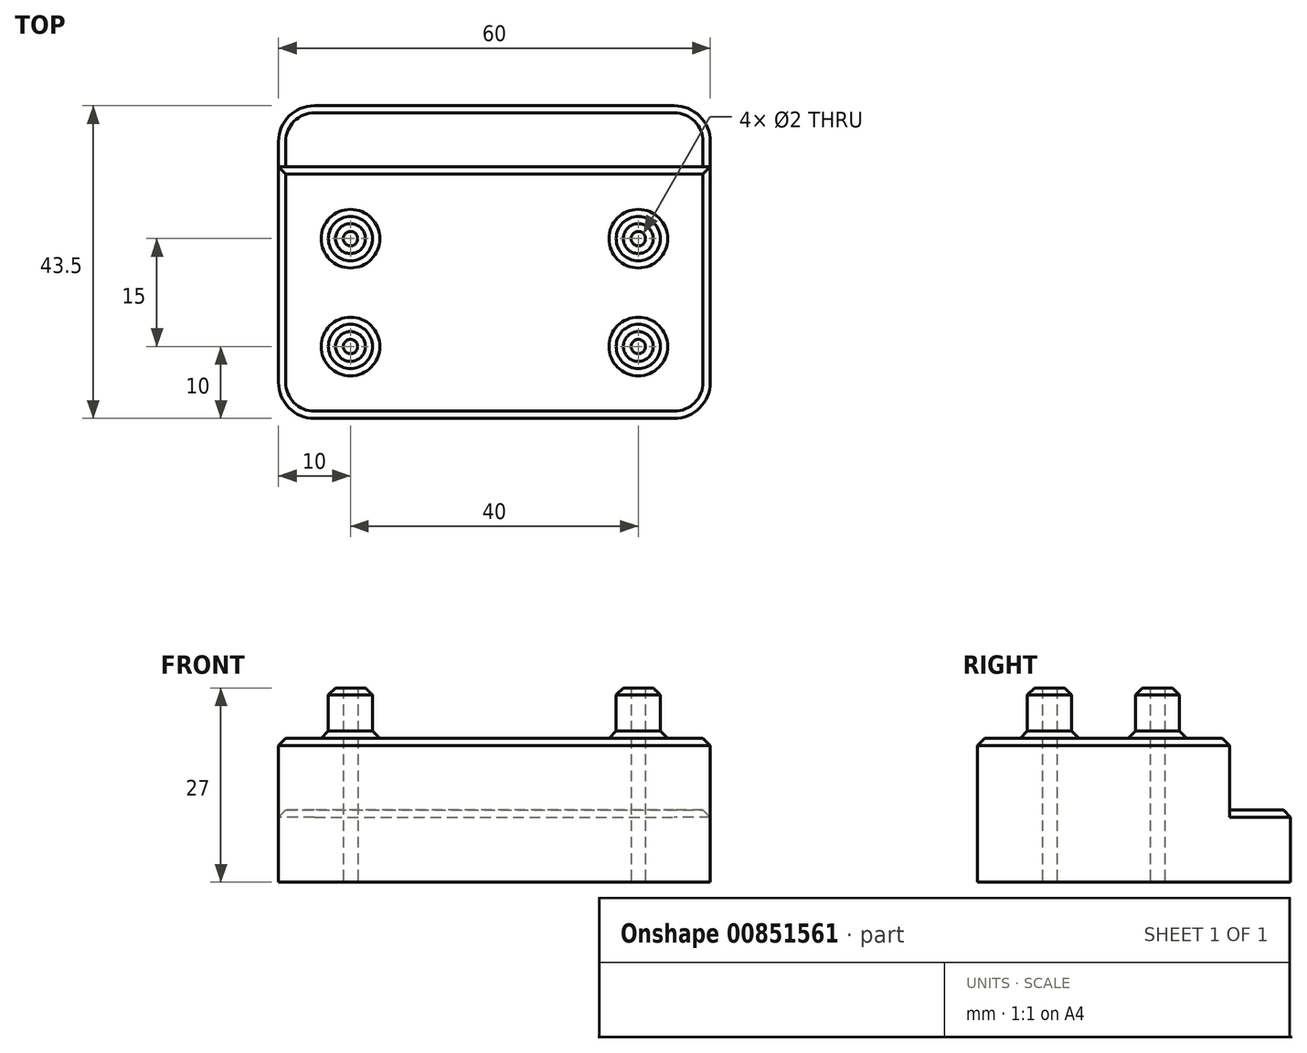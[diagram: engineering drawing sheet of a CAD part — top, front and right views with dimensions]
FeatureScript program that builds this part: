
annotation { "Feature Type Name" : "Feature", "Feature Type Description" : "" }
export const myFeature = defineFeature(function(context is Context, id is Id, definition is map)
    precondition{}
    {
        {
            var Q0;
            Q0=qCreatedBy(makeId("Top.planeOp"),FACE);
            var sketch = newSketch(context, id + "F0", { "sketchPlane" : qUnion([Q0])});
            skLineSegment(sketch, "E0.bottom", {"start": v(0, 0) * mm, "end": v(60, 0) * mm});
            skLineSegment(sketch, "E0.top", {"start": v(0, 43.5) * mm, "end": v(60, 43.5) * mm});
            skLineSegment(sketch, "E0.left", {"start": v(0, 0) * mm, "end": v(0, 43.5) * mm});
            skLineSegment(sketch, "E0.right", {"start": v(60, 0) * mm, "end": v(60, 43.5) * mm});
            skCircle(sketch, "E1", {"center": v(10, 10) * mm, "radius": 3.08 * mm});
            skCircle(sketch, "E2", {"center": v(10, 10) * mm, "radius": 1 * mm});
            skCircle(sketch, "E3.0.1.0", {"center": v(10, 25) * mm, "radius": 1 * mm});
            skCircle(sketch, "E3.0.1.1", {"center": v(10, 25) * mm, "radius": 3.08 * mm});
            skCircle(sketch, "E3.1.0.0", {"center": v(50, 10) * mm, "radius": 1 * mm});
            skCircle(sketch, "E3.1.0.1", {"center": v(50, 10) * mm, "radius": 3.08 * mm});
            skCircle(sketch, "E3.1.1.0", {"center": v(50, 25) * mm, "radius": 1 * mm});
            skCircle(sketch, "E3.1.1.1", {"center": v(50, 25) * mm, "radius": 3.08 * mm});
            skCircle(sketch, "E3.2.0.0", {"center": v(90, 10) * mm, "radius": 1 * mm});
            skCircle(sketch, "E3.2.0.1", {"center": v(90, 10) * mm, "radius": 3.08 * mm});
            skCircle(sketch, "E3.2.1.0", {"center": v(90, 25) * mm, "radius": 1 * mm});
            skCircle(sketch, "E3.2.1.1", {"center": v(90, 25) * mm, "radius": 3.08 * mm});
            skLineSegment(sketch, "E3.direction1", {"start": v(10, 10) * mm, "end": v(50, 10) * mm, "construction": true});
            skLineSegment(sketch, "E3.direction2", {"start": v(10, 10) * mm, "end": v(10, 25) * mm, "construction": true});
            skSolve(sketch);
        }
        {
            var Q0;
            Q0=makeQuery(id+"F0.imprint","IMPRINT",FACE,{"disambiguationData":[TD([[makeQuery(id+"F0.imprint","IMPRINT",EDGE,{"derivedFrom":sQuery(id+"F0.wireOp",EDGE,"E0.bottom")}),1.0]])]});
            extrude(context, id + "F1", {"entities" : qUnion([Q0]), "depth" : 20 * mm, "offsetDistance" : 25 * mm});
        }
        {
            var Q0;
            Q0=makeQuery(id+"F0.imprint","IMPRINT",FACE,{"disambiguationData":[TD([[makeQuery(id+"F0.imprint","IMPRINT",EDGE,{"derivedFrom":sQuery(id+"F0.wireOp",EDGE,"E3.0.1.0")}),-1.0]])]});
            var Q1;
            Q1=makeQuery(id+"F0.imprint","IMPRINT",FACE,{"disambiguationData":[TD([[makeQuery(id+"F0.imprint","IMPRINT",EDGE,{"derivedFrom":sQuery(id+"F0.wireOp",EDGE,"E1")}),1.0]])]});
            var Q2;
            Q2=makeQuery(id+"F0.imprint","IMPRINT",FACE,{"disambiguationData":[TD([[makeQuery(id+"F0.imprint","IMPRINT",EDGE,{"derivedFrom":sQuery(id+"F0.wireOp",EDGE,"E3.1.0.0")}),-1.0]])]});
            var Q3;
            Q3=makeQuery(id+"F0.imprint","IMPRINT",FACE,{"disambiguationData":[TD([[makeQuery(id+"F0.imprint","IMPRINT",EDGE,{"derivedFrom":sQuery(id+"F0.wireOp",EDGE,"E3.1.1.0")}),-1.0]])]});
            var Q4;
            Q4=sQuery(id+"F0.wireOp",EDGE,"E3.0.1.1");
            var Q5;
            Q5=sQuery(id+"F0.wireOp",EDGE,"E1");
            var Q6;
            Q6=sQuery(id+"F0.wireOp",EDGE,"E3.1.0.1");
            var Q7;
            Q7=sQuery(id+"F0.wireOp",EDGE,"E3.1.1.1");
            extrude(context, id + "F2", {"entities" : qUnion([Q0, Q1, Q2, Q3]), "operationType" : NewBodyOperationType.ADD, "surfaceOperationType" : NewSurfaceOperationType.ADD, "surfaceEntities" : qUnion([Q4, Q5, Q6, Q7]), "depth" : 27 * mm, "offsetDistance" : 25 * mm});
        }
        {
            var Q0;
            Q0=makeQuery(id+"F1.opExtrude","CAP_FACE",FACE,{"disambiguationData":[OSD([sQuery(id+"F0.wireOp",EDGE,"E0.bottom"),sQuery(id+"F0.wireOp",EDGE,"E0.top"),sQuery(id+"F0.wireOp",EDGE,"E0.left"),sQuery(id+"F0.wireOp",EDGE,"E0.right"),sQuery(id+"F0.wireOp",EDGE,"E1"),sQuery(id+"F0.wireOp",EDGE,"E3.0.1.1"),sQuery(id+"F0.wireOp",EDGE,"E3.1.0.1"),sQuery(id+"F0.wireOp",EDGE,"E3.1.1.1")])],"isStart":false});
            var sketch = newSketch(context, id + "F3", { "sketchPlane" : qUnion([Q0])});
            skLineSegment(sketch, "E4.bottom", {"start": v(0, 43.5) * mm, "end": v(60, 43.5) * mm});
            skLineSegment(sketch, "E4.top", {"start": v(0, 35) * mm, "end": v(60, 35) * mm});
            skLineSegment(sketch, "E4.left", {"start": v(0, 43.5) * mm, "end": v(0, 35) * mm});
            skLineSegment(sketch, "E4.right", {"start": v(60, 43.5) * mm, "end": v(60, 35) * mm});
            skSolve(sketch);
        }
        {
            var Q0;
            Q0=makeQuery(id+"F3.imprint","IMPRINT",FACE,{"disambiguationData":[TD([[makeQuery(id+"F3.imprint","IMPRINT",EDGE,{"derivedFrom":sQuery(id+"F3.wireOp",EDGE,"E4.bottom")}),-1.0]])]});
            extrude(context, id + "F4", {"entities" : qUnion([Q0]), "operationType" : NewBodyOperationType.REMOVE, "oppositeDirection" : true, "depth" : 10 * mm, "offsetDistance" : 25 * mm});
        }
        {
            var Q0;
            Q0=makeQuery(id+"F1.opExtrude","SWEPT_EDGE",EDGE,{"disambiguationData":[OSD([sQuery(id+"F0.wireOp",EDGE,"E0.bottom"),sQuery(id+"F0.wireOp",EDGE,"E0.right")])]});
            var Q1;
            Q1=makeQuery(id+"F1.opExtrude","SWEPT_EDGE",EDGE,{"disambiguationData":[OSD([sQuery(id+"F0.wireOp",EDGE,"E0.bottom"),sQuery(id+"F0.wireOp",EDGE,"E0.left")])]});
            var Q2;
            Q2=makeQuery(id+"F1.opExtrude","SWEPT_EDGE",EDGE,{"disambiguationData":[OSD([sQuery(id+"F0.wireOp",EDGE,"E0.top"),sQuery(id+"F0.wireOp",EDGE,"E0.right")])]});
            var Q3;
            Q3=makeQuery(id+"F4.boolean.opBoolean","COPY",EDGE,{"derivedFrom":makeQuery(id+"F4.opExtrude","SWEPT_EDGE",EDGE,{"disambiguationData":[OSD([sQuery(id+"F0.wireOp",EDGE,"E0.right"),sQuery(id+"F3.wireOp",EDGE,"E4.top"),sQuery(id+"F3.wireOp",EDGE,"E4.right")])]})});
            var Q4;
            Q4=makeQuery(id+"F4.boolean.opBoolean","COPY",EDGE,{"derivedFrom":makeQuery(id+"F4.opExtrude","SWEPT_EDGE",EDGE,{"disambiguationData":[OSD([sQuery(id+"F0.wireOp",EDGE,"E0.left"),sQuery(id+"F3.wireOp",EDGE,"E4.top"),sQuery(id+"F3.wireOp",EDGE,"E4.left")])]})});
            var Q5;
            Q5=makeQuery(id+"F1.opExtrude","SWEPT_EDGE",EDGE,{"disambiguationData":[OSD([sQuery(id+"F0.wireOp",EDGE,"E0.top"),sQuery(id+"F0.wireOp",EDGE,"E0.left")])]});
            fillet(context, id + "F5", {"entities" : qUnion([Q0, Q1, Q2, Q3, Q4, Q5]), "radius" : 5 * mm, "tangentPropagation" : true, "allowEdgeOverflow" : false});
        }
        {
            var Q0;
            Q0=makeQuery(id+"F1.opExtrude","CAP_FACE",FACE,{"disambiguationData":[OSD([sQuery(id+"F0.wireOp",EDGE,"E0.bottom"),sQuery(id+"F0.wireOp",EDGE,"E0.top"),sQuery(id+"F0.wireOp",EDGE,"E0.left"),sQuery(id+"F0.wireOp",EDGE,"E0.right"),sQuery(id+"F0.wireOp",EDGE,"E1"),sQuery(id+"F0.wireOp",EDGE,"E3.0.1.1"),sQuery(id+"F0.wireOp",EDGE,"E3.1.0.1"),sQuery(id+"F0.wireOp",EDGE,"E3.1.1.1")])],"isStart":false});
            var Q1;
            Q1=makeQuery(id+"F2.opExtrude","CAP_EDGE",EDGE,{"disambiguationData":[OSD([sQuery(id+"F0.wireOp",EDGE,"E1")])],"isStart":false});
            var Q2;
            Q2=makeQuery(id+"F2.opExtrude","CAP_EDGE",EDGE,{"disambiguationData":[OSD([sQuery(id+"F0.wireOp",EDGE,"E3.0.1.1")])],"isStart":false});
            var Q3;
            Q3=makeQuery(id+"F2.opExtrude","CAP_EDGE",EDGE,{"disambiguationData":[OSD([sQuery(id+"F0.wireOp",EDGE,"E3.1.1.1")])],"isStart":false});
            var Q4;
            Q4=makeQuery(id+"F2.opExtrude","CAP_EDGE",EDGE,{"disambiguationData":[OSD([sQuery(id+"F0.wireOp",EDGE,"E3.1.0.1")])],"isStart":false});
            var Q5;
            Q5=makeQuery(id+"F4.boolean.opBoolean","COPY",EDGE,{"derivedFrom":makeQuery(id+"F4.opExtrude","CAP_EDGE",EDGE,{"disambiguationData":[OSD([sQuery(id+"F3.wireOp",EDGE,"E4.bottom")])],"isStart":false})});
            var Q6;
            Q6=makeQuery(id+"F5.opFillet","BLEND_EDGE",EDGE,{"blendedFrom":[makeQuery(id+"F1.opExtrude","SWEPT_EDGE",EDGE,{"disambiguationData":[OSD([sQuery(id+"F0.wireOp",EDGE,"E0.top"),sQuery(id+"F0.wireOp",EDGE,"E0.right")])]}),makeQuery(id+"F4.boolean.opBoolean","COPY",FACE,{"derivedFrom":makeQuery(id+"F4.opExtrude","CAP_FACE",FACE,{"disambiguationData":[OSD([sQuery(id+"F3.wireOp",EDGE,"E4.bottom"),sQuery(id+"F3.wireOp",EDGE,"E4.top"),sQuery(id+"F3.wireOp",EDGE,"E4.left"),sQuery(id+"F3.wireOp",EDGE,"E4.right")])],"isStart":false})})],"blendedInto":[makeQuery(id+"F4.boolean.opBoolean","COPY",FACE,{"derivedFrom":makeQuery(id+"F4.opExtrude","CAP_FACE",FACE,{"disambiguationData":[OSD([sQuery(id+"F3.wireOp",EDGE,"E4.bottom"),sQuery(id+"F3.wireOp",EDGE,"E4.top"),sQuery(id+"F3.wireOp",EDGE,"E4.left"),sQuery(id+"F3.wireOp",EDGE,"E4.right")])],"isStart":false})})]});
            chamfer(context, id + "F6", {"entities" : qUnion([Q0, Q1, Q2, Q3, Q4, Q5, Q6]), "width" : 1 * mm, "tangentPropagation" : true});
        }
    });
